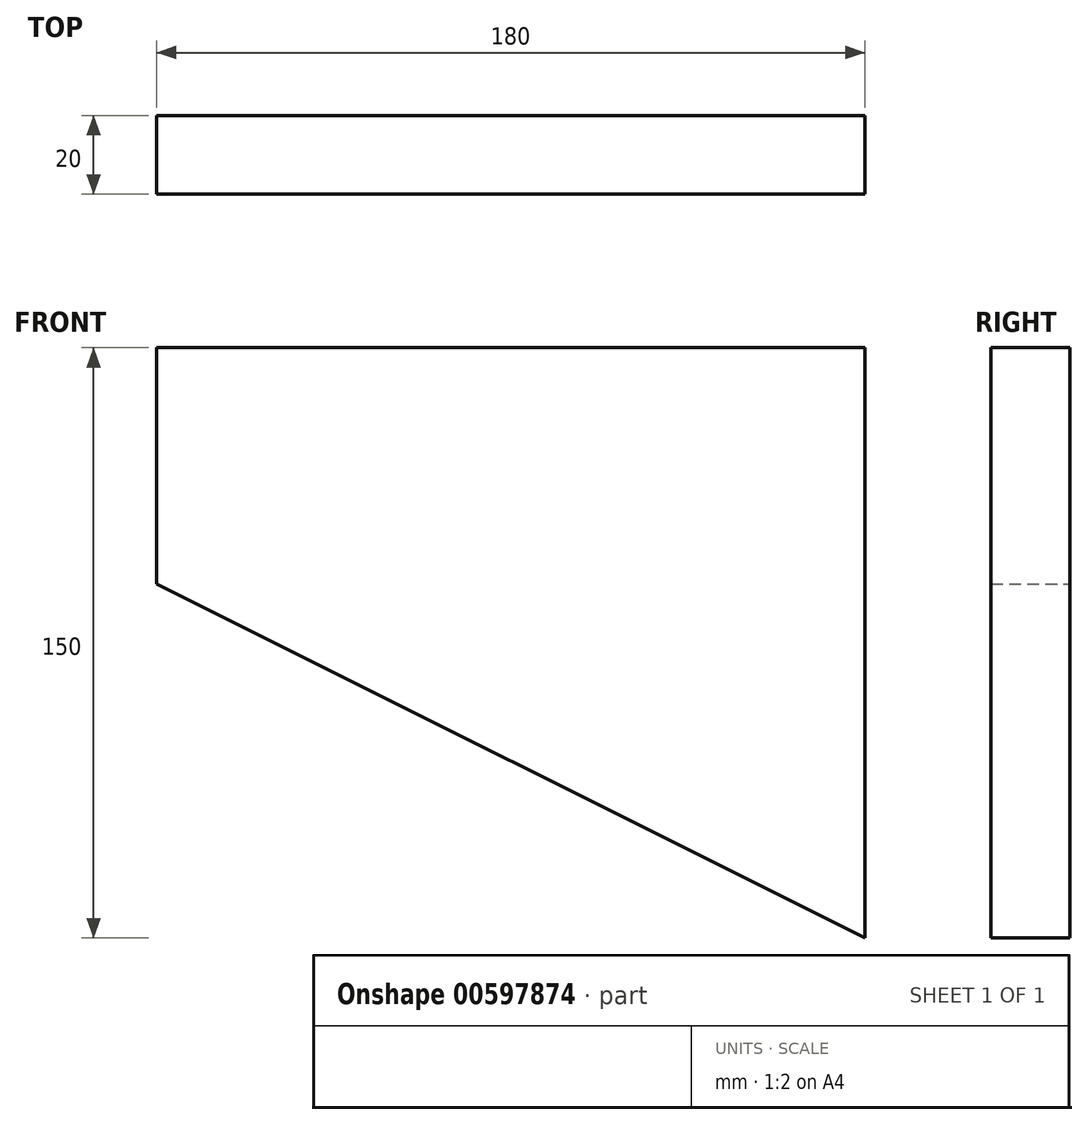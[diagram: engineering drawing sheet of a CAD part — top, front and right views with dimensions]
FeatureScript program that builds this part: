
annotation { "Feature Type Name" : "Feature", "Feature Type Description" : "" }
export const myFeature = defineFeature(function(context is Context, id is Id, definition is map)
    precondition{}
    {
        {
            var Q0;
            Q0=qCreatedBy(makeId("Front.planeOp"),FACE);
            var sketch = newSketch(context, id + "F0", { "sketchPlane" : qUnion([Q0])});
            skLineSegment(sketch, "E0", {"start": v(0, 0) * mm, "end": v(0, 150) * mm});
            skLineSegment(sketch, "E1", {"start": v(0, 150) * mm, "end": v(-180, 150) * mm});
            skLineSegment(sketch, "E2", {"start": v(-180, 150) * mm, "end": v(-180, 90) * mm});
            skLineSegment(sketch, "E3", {"start": v(-180, 90) * mm, "end": v(0, 0) * mm});
            skSolve(sketch);
        }
        {
            var Q0;
            Q0=qSketchRegion(id+"F0",true);
            extrude(context, id + "F1", {"entities" : qUnion([Q0]), "depth" : 20 * mm});
        }
    });
